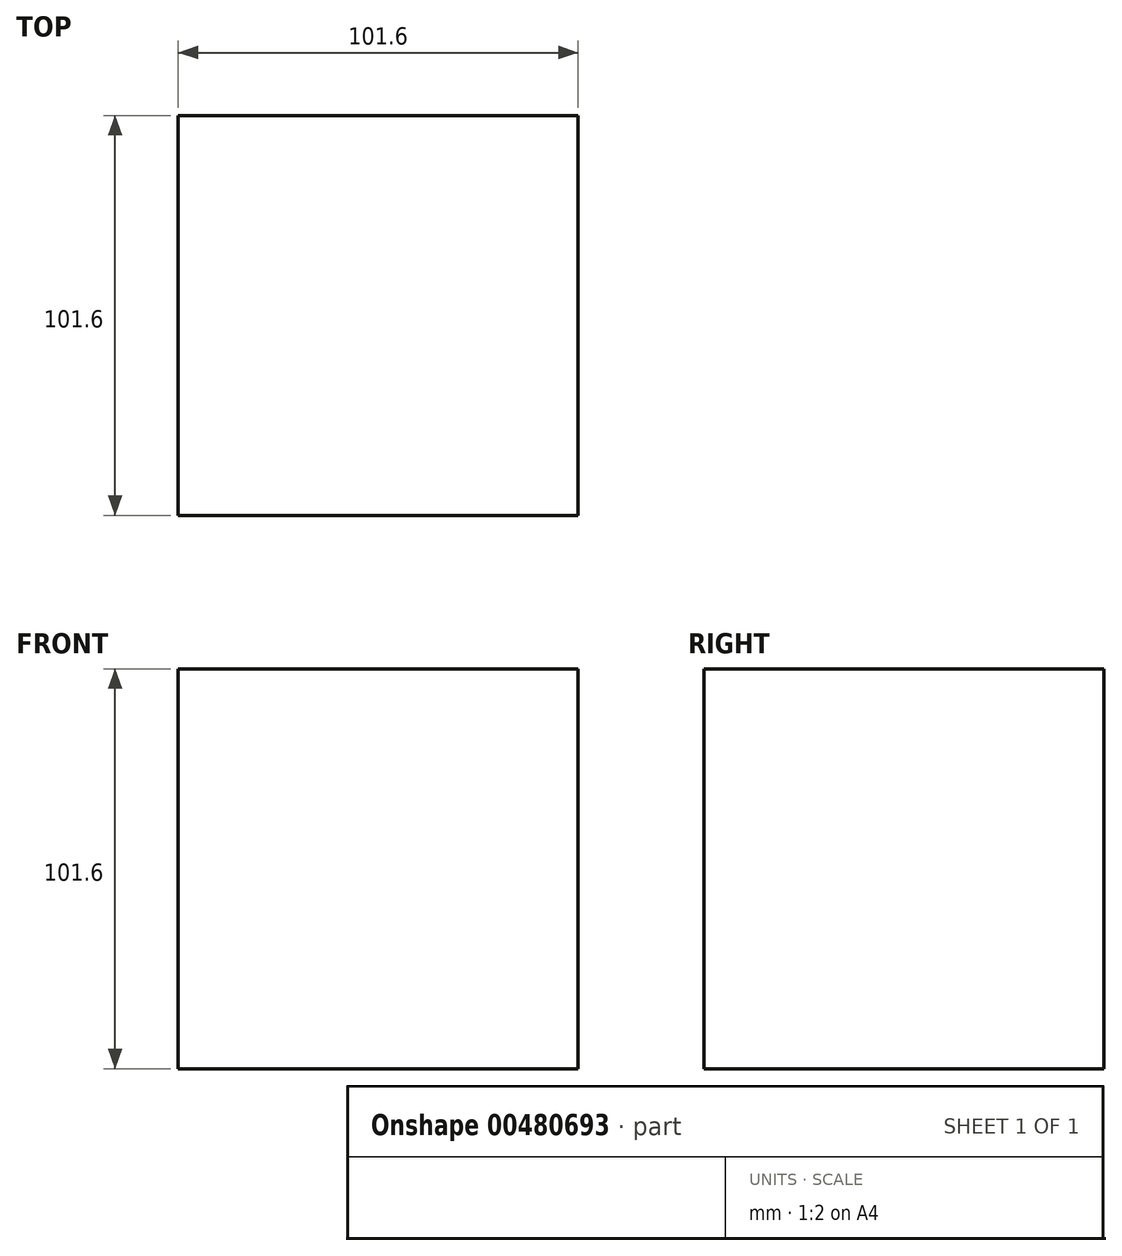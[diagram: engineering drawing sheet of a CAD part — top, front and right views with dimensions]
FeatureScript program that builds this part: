
annotation { "Feature Type Name" : "Feature", "Feature Type Description" : "" }
export const myFeature = defineFeature(function(context is Context, id is Id, definition is map)
    precondition{}
    {
        {
            var Q0;
            Q0=qCreatedBy(makeId("Front.planeOp"),FACE);
            var sketch = newSketch(context, id + "F0", { "sketchPlane" : qUnion([Q0])});
            skLineSegment(sketch, "E0", {"start": v(-50.8, 0) * mm, "end": v(-50.8, 50.8) * mm});
            skLineSegment(sketch, "E1", {"start": v(-50.8, 0) * mm, "end": v(-50.8, -50.8) * mm});
            skLineSegment(sketch, "E2", {"start": v(-50.8, 50.8) * mm, "end": v(0, 50.8) * mm});
            skLineSegment(sketch, "E3", {"start": v(-50.8, -50.8) * mm, "end": v(0, -50.8) * mm});
            skLineSegment(sketch, "E4.MirrorCS", {"start": v(50.8, 50.8) * mm, "end": v(0, 50.8) * mm});
            skLineSegment(sketch, "E5.MirrorCS", {"start": v(50.8, 0) * mm, "end": v(50.8, 50.8) * mm});
            skLineSegment(sketch, "E6.MirrorCS", {"start": v(50.8, 0) * mm, "end": v(50.8, -50.8) * mm});
            skLineSegment(sketch, "E7.MirrorCS", {"start": v(50.8, -50.8) * mm, "end": v(0, -50.8) * mm});
            skLineSegment(sketch, "E8", {"start": v(0, 50.8) * mm, "end": v(0, -50.8) * mm});
            skLineSegment(sketch, "E9.bottom", {"start": v(36.61, 50.8) * mm, "end": v(31.88, 50.8) * mm});
            skLineSegment(sketch, "E9.top", {"start": v(36.61, -50.8) * mm, "end": v(31.88, -50.8) * mm});
            skLineSegment(sketch, "E9.left", {"start": v(36.61, 50.8) * mm, "end": v(36.61, -50.8) * mm});
            skLineSegment(sketch, "E9.right", {"start": v(31.88, 50.8) * mm, "end": v(31.88, -50.8) * mm});
            skLineSegment(sketch, "E10.bottom", {"start": v(14.83, 50.8) * mm, "end": v(20.83, 50.8) * mm});
            skLineSegment(sketch, "E10.top", {"start": v(14.83, -50.8) * mm, "end": v(20.83, -50.8) * mm});
            skLineSegment(sketch, "E10.left", {"start": v(14.83, 50.8) * mm, "end": v(14.83, -50.8) * mm});
            skLineSegment(sketch, "E10.right", {"start": v(20.83, 50.8) * mm, "end": v(20.83, -50.8) * mm});
            skLineSegment(sketch, "E11.bottom", {"start": v(-25.4, 50.8) * mm, "end": v(-19.88, 50.8) * mm});
            skLineSegment(sketch, "E11.top", {"start": v(-25.4, -50.8) * mm, "end": v(-19.88, -50.8) * mm});
            skLineSegment(sketch, "E11.left", {"start": v(-25.4, 50.8) * mm, "end": v(-25.4, -50.8) * mm});
            skLineSegment(sketch, "E11.right", {"start": v(-19.88, 50.8) * mm, "end": v(-19.88, -50.8) * mm});
            skSolve(sketch);
        }
        {
            var Q0;
            Q0 = qSketchRegion(id + "F0", true);
            extrude(context, id + "F1", {"entities" : qUnion([Q0]), "depth" : 101.6 * mm});
        }
    });
